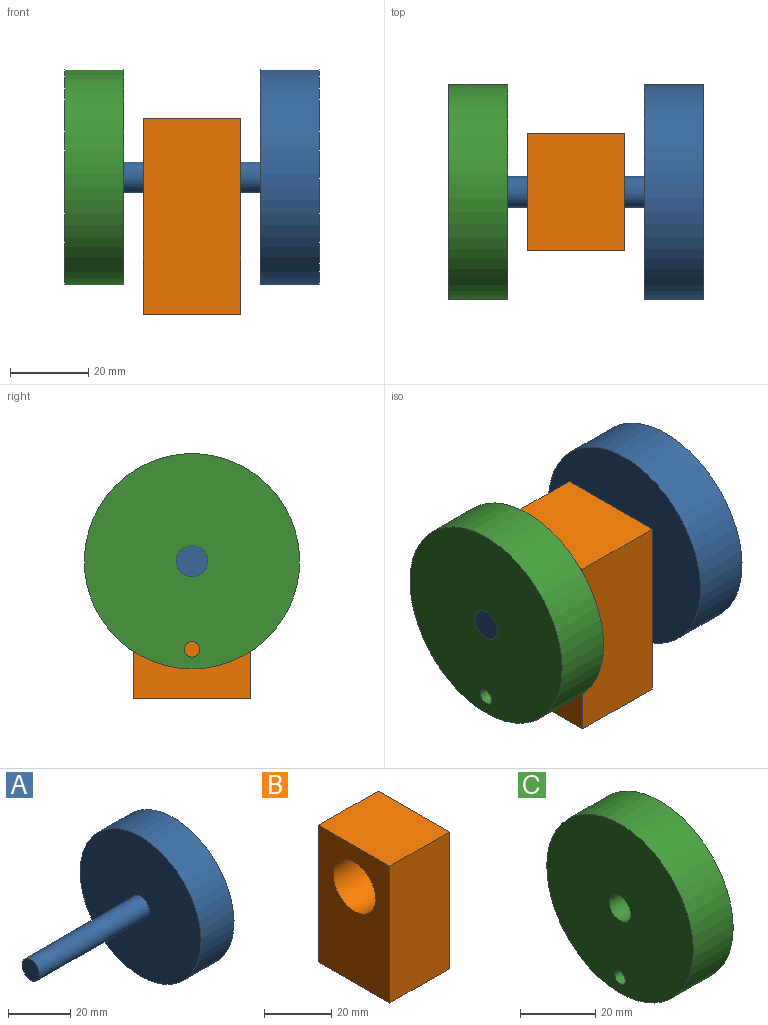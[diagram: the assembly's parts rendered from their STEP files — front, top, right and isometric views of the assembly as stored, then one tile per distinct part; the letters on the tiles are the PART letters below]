
ASSEMBLY  parts=3 mates=2
PART A: 7 faces, bbox 65x55x55 mm
  f0: cylinder r=1.5mm len=10mm, axis (-1,0,0), area 94.2mm2, adj f2,f6
  f1: cylinder r=27.5mm len=55mm, axis (-1,0,0), area 2591.8mm2, adj f2,f3
  f2: plane 55x55mm, normal (1,0,0), area 2368.8mm2, adj f0,f1
  f3: plane 55x55mm, normal (-1,0,0), area 2325.6mm2, adj f1,f4
  f4: cylinder r=4mm len=50mm, axis (1,0,0), area 1256.6mm2, adj f3,f5
  f5: plane 8x8mm, normal (-1,0,0), area 50.3mm2, adj f4
  f6: plane 3x3mm, normal (1,0,0), area 7.1mm2, adj f0
PART B: 7 faces, bbox 25x30x50 mm
  f0: plane 50x25mm, normal (0,-1,0), area 1250mm2, adj f1,f4,f5,f6
  f1: plane 30x25mm, normal (0,0,-1), area 750mm2, adj f0,f2,f5,f6
  f2: plane 50x25mm, normal (0,1,0), area 1250mm2, adj f1,f4,f5,f6
  f3: cylinder r=9mm len=25mm, axis (-1,0,0), area 1413.7mm2, adj f5,f6
  f4: plane 30x25mm, normal (0,0,1), area 750mm2, adj f0,f2,f5,f6
  f5: plane 50x30mm, normal (1,0,0), area 1245.5mm2, adj f0,f1,f2,f3,f4
  f6: plane 50x30mm, normal (-1,0,0), area 1245.5mm2, adj f0,f1,f2,f3,f4
PART C: 5 faces, bbox 15x55x55 mm
  f0: cylinder r=2mm len=15mm, axis (-1,0,0), area 188.5mm2, adj f3,f4
  f1: cylinder r=4mm len=15mm, axis (-1,0,0), area 377mm2, adj f3,f4
  f2: cylinder r=27.5mm len=55mm, axis (-1,0,0), area 2591.8mm2, adj f3,f4
  f3: plane 55x55mm, normal (1,0,0), area 2313mm2, adj f0,f1,f2
  f4: plane 55x55mm, normal (-1,0,0), area 2313mm2, adj f0,f1,f2
PLACE A rot(axis=(1,0,0),0deg) t=(90.24,-29.98,51.48)mm
PLACE B t=(60.24,-29.98,16.48)mm fixed
PLACE C rot(axis=(1,0,0),0deg) t=(40.24,-29.98,51.48)mm
MATE revolute A.f4 <-> C.f2  axis (-1,0,0) through (40.24,-29.98,51.48)mm
MATE revolute C.f1 <-> B.f3  axis (-1,0,0) through (40.24,-29.98,51.48)mm
